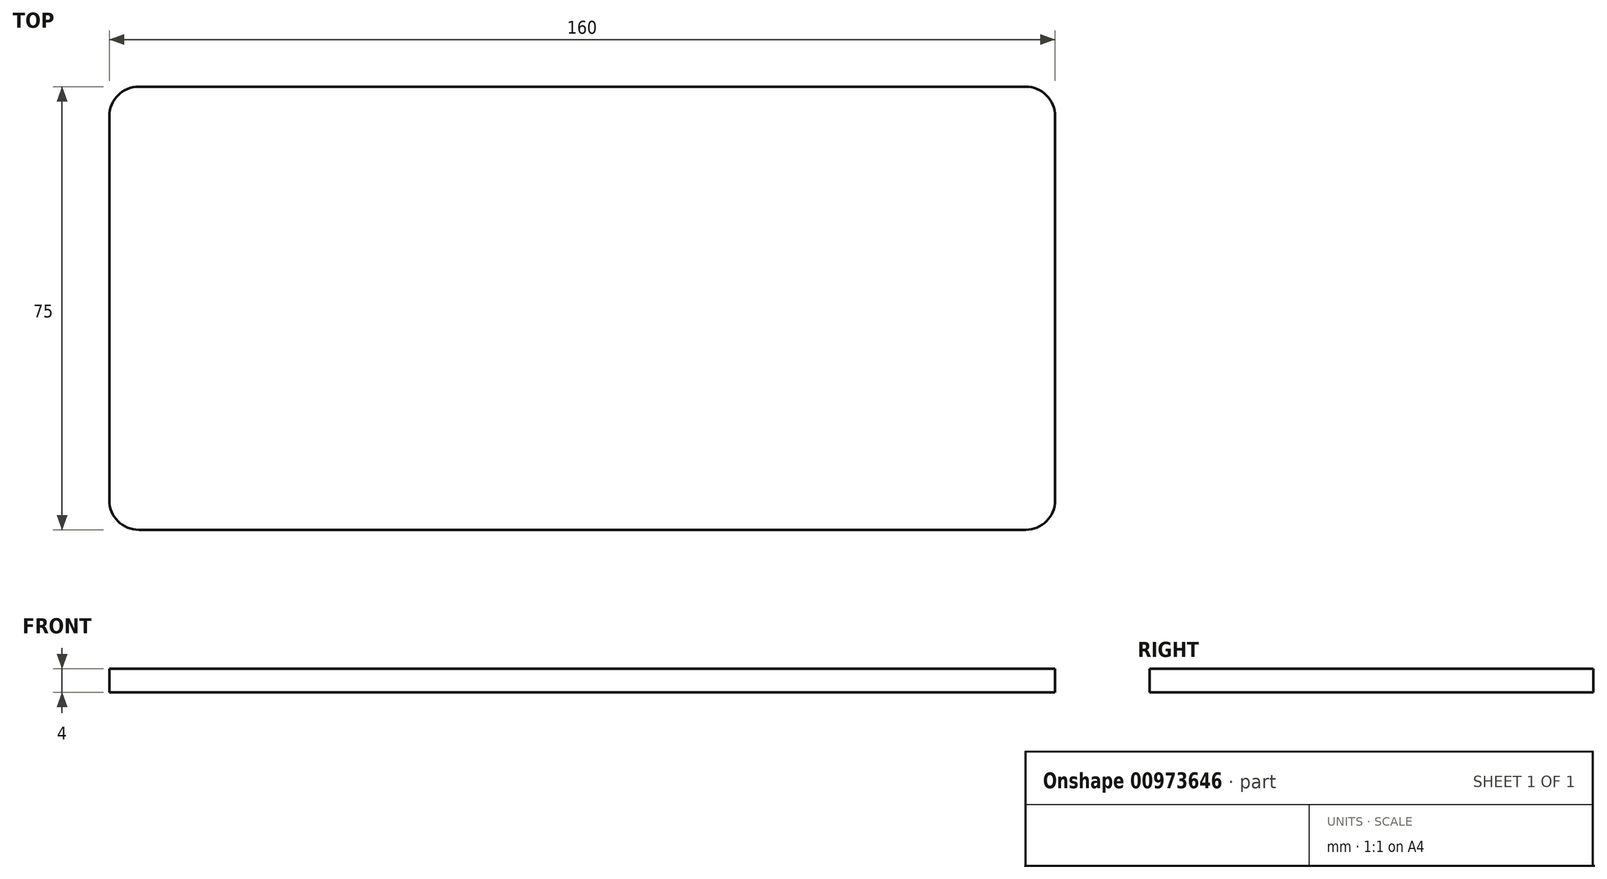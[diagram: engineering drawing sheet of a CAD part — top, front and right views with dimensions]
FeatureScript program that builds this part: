
annotation { "Feature Type Name" : "Feature", "Feature Type Description" : "" }
export const myFeature = defineFeature(function(context is Context, id is Id, definition is map)
    precondition{}
    {
        {
            var Q0;
            Q0=qCreatedBy(makeId("Top.planeOp"),FACE);
            var sketch = newSketch(context, id + "F0", { "sketchPlane" : qUnion([Q0])});
            skLineSegment(sketch, "E0", {"start": v(-5, 0) * mm, "end": v(-155, 0) * mm});
            skLineSegment(sketch, "E1", {"start": v(-160, -5) * mm, "end": v(-160, -70) * mm});
            skLineSegment(sketch, "E2", {"start": v(-155, -75) * mm, "end": v(-5, -75) * mm});
            skLineSegment(sketch, "E3", {"start": v(0, -70) * mm, "end": v(0, -5) * mm});
            skPoint(sketch, "E4.visualSharp", {"position": v(-160, 0) * mm});
            skArc(sketch, "E4.filletArc", {"start": v(-155, 0) * mm, "mid": v(-158.54, -1.46) * mm, "end": v(-160, -5) * mm});
            skPoint(sketch, "E5.visualSharp", {"position": v(0, 0) * mm});
            skArc(sketch, "E5.filletArc", {"start": v(0, -5) * mm, "mid": v(-1.46, -1.46) * mm, "end": v(-5, 0) * mm});
            skPoint(sketch, "E6.visualSharp", {"position": v(0, -75) * mm});
            skArc(sketch, "E6.filletArc", {"start": v(-5, -75) * mm, "mid": v(-1.46, -73.54) * mm, "end": v(0, -70) * mm});
            skPoint(sketch, "E7.visualSharp", {"position": v(-160, -75) * mm});
            skArc(sketch, "E7.filletArc", {"start": v(-160, -70) * mm, "mid": v(-158.54, -73.54) * mm, "end": v(-155, -75) * mm});
            skSolve(sketch);
        }
        {
            var Q0;
            Q0=makeQuery(id+"F0.imprint","IMPRINT",FACE,{"disambiguationData":[TD([[makeQuery(id+"F0.imprint","IMPRINT",EDGE,{"derivedFrom":sQuery(id+"F0.wireOp",EDGE,"E0")}),1.0]])]});
            extrude(context, id + "F1", {"entities" : qUnion([Q0]), "depth" : 4 * mm, "offsetDistance" : 25 * mm});
        }
    });
